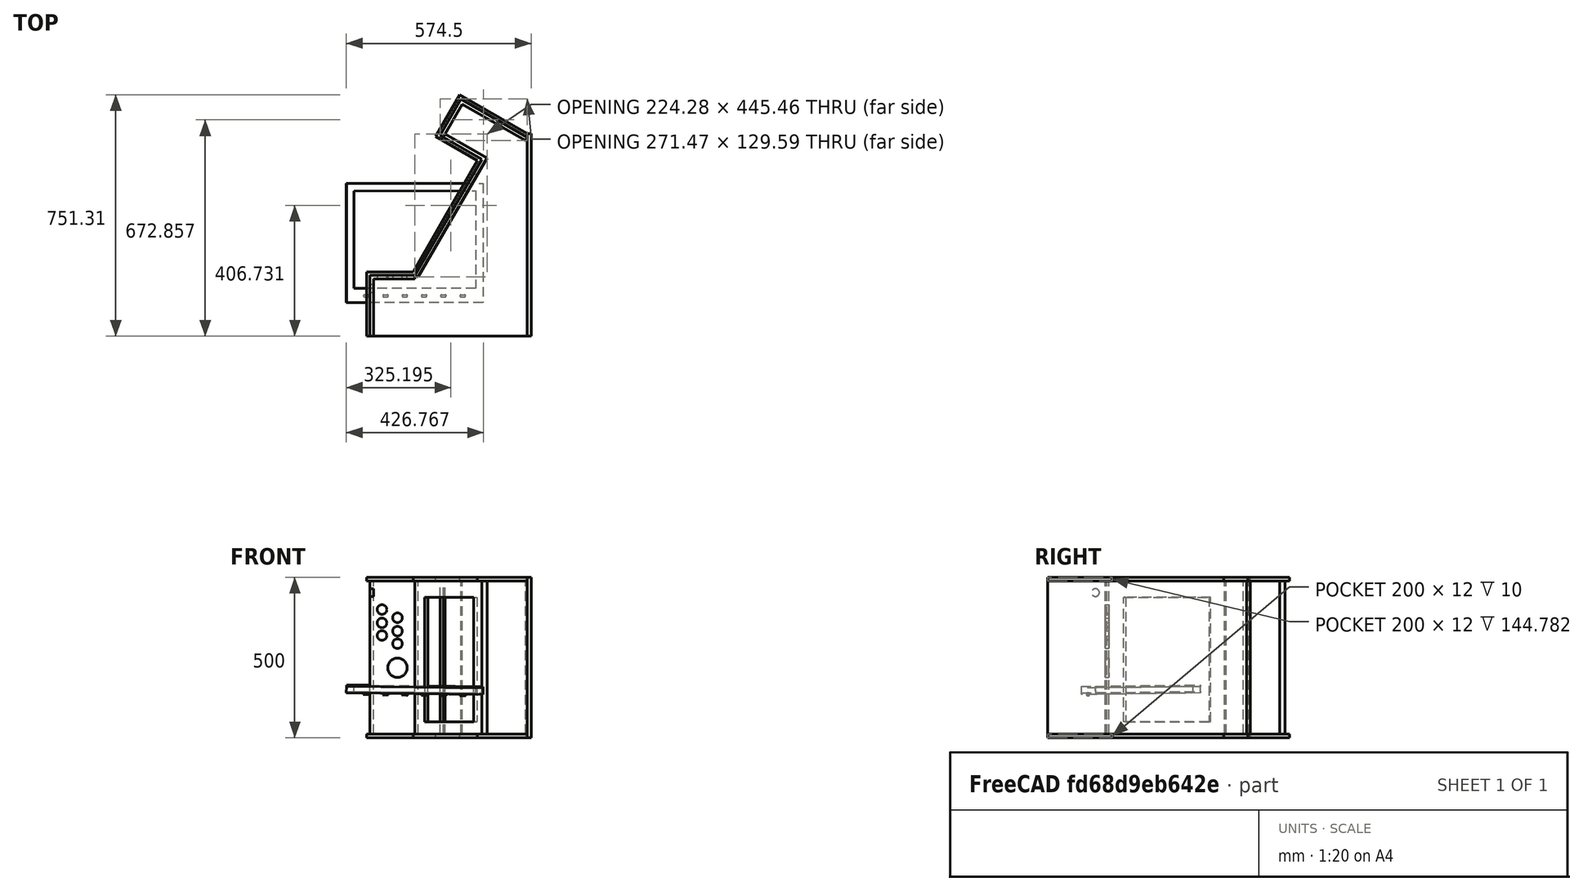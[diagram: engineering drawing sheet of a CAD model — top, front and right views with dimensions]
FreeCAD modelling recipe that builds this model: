
FCSTD DOCUMENT  (FreeCAD 0.17R13541 (Git))
Label: arcadeAvecHautDECO
License: All rights reserved
LicenseURL: http://en.wikipedia.org/wiki/All_rights_reserved
objects: TechDraw::DrawViewDimension×23, Sketcher::SketchObject×8, PartDesign::Pad×5, TechDraw::DrawViewPart×5, Image::ImagePlane×4, PartDesign::Plane×3, PartDesign::Pocket×3, PartDesign::LinearPattern×2, PartDesign::Body×2, TechDraw::DrawViewAnnotation×2, TechDraw::DrawSVGTemplate×1, TechDraw::DrawPage×1
note: 31 computed .brp shape members not serialized (recipe doc carries the construction recipe); baked Part::Feature solids carry a one-line shape summary decoded from their .brp

FEATURE [Sketcher::SketchObject] Sketch  label="coteGauche"
  MapMode = 5
  Support = -> [XY_Plane]
  sketch-geometry (10):
    g0: LineSegment StartX=-500 StartY=200 StartZ=0 EndX=-500 EndY=0 EndZ=0
    g1: LineSegment StartX=-500 StartY=0 StartZ=0 EndX=0 EndY=0 EndZ=0
    g2: LineSegment StartX=0 StartY=0 StartZ=0 EndX=0 EndY=546.41 EndZ=0
    g3: LineSegment [constr] StartX=0 StartY=546.41 StartZ=0 EndX=-155.218 EndY=546.41 EndZ=0
    g4: LineSegment StartX=-155.218 StartY=546.41 StartZ=0 EndX=-355.218 EndY=200 EndZ=0
    g5: LineSegment StartX=-355.218 StartY=200 StartZ=0 EndX=-500 EndY=200 EndZ=0
    g6: LineSegment StartX=-155.218 StartY=546.41 StartZ=0 EndX=-285.122 EndY=621.41 EndZ=0
    g7: LineSegment StartX=-285.122 StartY=621.41 StartZ=0 EndX=-210.122 EndY=751.314 EndZ=0
    g8: LineSegment StartX=-210.122 StartY=751.314 StartZ=0 EndX=0 EndY=630 EndZ=0
    g9: LineSegment StartX=0 StartY=630 StartZ=0 EndX=0 EndY=546.41 EndZ=0
  constraints (28):
    c: Vertical(g0)
    c: Coincident(g0,g1)
    c: Horizontal(g1)
    c: Coincident(g1,g2)
    c: Vertical(g2)
    c: Coincident(g2,g3)
    c: Horizontal(g3)
    c: Coincident(g3,g4)
    c: Coincident(g5,g0)
    c: DistanceX(g1,g1) = 500
    c: DistanceY(g0,g0) = 200
    c: Horizontal(g5)
    c: Coincident(g4,g5)
    c: Coincident(g1,g-1)
    c: Angle(g4,g3) = 2.0944
    c: Distance(g4) = 400
    c: Coincident(g6,g3)
    c: Coincident(g7,g6)
    c: Coincident(g8,g7)
    c: PointOnObject(g8,g-2)
    c: Coincident(g9,g8)
    c: Coincident(g9,g2)
    c: Perpendicular(g6,g7)
    c: Perpendicular(g7,g8)
    c: Perpendicular(g6,g4)
    c: Distance(g6) = 150
    c: Distance(g7) = 150
    c: DistanceY(g1,g8) = 630
FEATURE [PartDesign::Pad] Pad
  Length = 12
  Length2 = 120
  Profile = -> Sketch
  Type = 0
FEATURE [Sketcher::SketchObject] Sketch002  label="arriere"
  ExternalGeometry = -> [Sketch]
  MapMode = 5
  Placement = pos=(0,0,0) rot=(0.57735,0.57735,0.57735;2.0944rad)
  Support = -> [YZ_Plane]
  sketch-geometry (4):
    g0: LineSegment StartX=0 StartY=0 StartZ=0 EndX=0 EndY=500 EndZ=0
    g1: LineSegment StartX=0 StartY=0 StartZ=0 EndX=630 EndY=0 EndZ=0
    g2: LineSegment StartX=630 StartY=0 StartZ=0 EndX=630 EndY=500 EndZ=0
    g3: LineSegment StartX=630 StartY=500 StartZ=0 EndX=0 EndY=500 EndZ=0
  constraints (10):
    c: Vertical(g0)
    c: DistanceY(g0,g0) = 500
    c: Coincident(g0,g-1)
    c: Coincident(g1,g-5)
    c: Coincident(g1,g2)
    c: Vertical(g2)
    c: Coincident(g2,g3)
    c: Coincident(g3,g0)
    c: Perpendicular(g2,g3)
    c: Coincident(g1,g0)
FEATURE [PartDesign::Pad] Pad001
  BaseFeature = -> Pad
  Length = 12
  Length2 = 120
  Profile = -> Sketch002
  Type = 0
FEATURE [PartDesign::LinearPattern] LinearPattern  label="coteDroit"
  BaseFeature = -> Pad001
  Direction = -> Z_Axis
  Length = 488
  Occurrences = 2
  Originals = -> [Pad]
FEATURE [Sketcher::SketchObject] Sketch003  label="Interieur"
  ExternalGeometry = -> [Sketch]
  MapMode = 5
  Support = -> [XY_Plane]
  sketch-geometry (39):
    g0: LineSegment StartX=-490 StartY=190 StartZ=0 EndX=-349.445 EndY=190 EndZ=0
    g1: LineSegment StartX=-349.445 StartY=190 StartZ=0 EndX=-141.558 EndY=550.07 EndZ=0
    g2: LineSegment StartX=-131.166 StartY=544.07 StartZ=0 EndX=-261.069 EndY=619.07 EndZ=0
    g3: LineSegment StartX=-271.465 StartY=625.064 StartZ=0 EndX=-206.462 EndY=737.654 EndZ=0
    g4: LineSegment StartX=-255.069 StartY=629.463 StartZ=0 EndX=-125.166 EndY=554.463 EndZ=0
    g5: LineSegment StartX=-131.166 StartY=544.07 StartZ=0 EndX=-339.052 EndY=184 EndZ=0
    g6: LineSegment StartX=-349.445 StartY=178 StartZ=0 EndX=-490 EndY=178 EndZ=0
    g7: LineSegment StartX=-478 StartY=178 StartZ=0 EndX=-478 EndY=0 EndZ=0
    g8: LineSegment StartX=-478 StartY=0 StartZ=0 EndX=-490 EndY=0 EndZ=0
    g9: LineSegment StartX=-490 StartY=0 StartZ=0 EndX=-490 EndY=178 EndZ=0
    g10: LineSegment StartX=-196.069 StartY=731.654 StartZ=0 EndX=0 EndY=618.453 EndZ=0
    g11: LineSegment StartX=-6 StartY=608.061 StartZ=0 EndX=-202.069 EndY=721.261 EndZ=0
    g12: LineSegment StartX=-196.069 StartY=731.654 StartZ=0 EndX=-261.073 EndY=619.064 EndZ=0
    g13: LineSegment [constr] StartX=-263.064 StartY=426.451 StartZ=0 EndX=-129.787 EndY=349.503 EndZ=0
    g14: GeomPoint X=-225.463 Y=404.742 Z=0
    g15: GeomPoint X=-215.071 Y=398.742 Z=0
    g16: LineSegment [constr] StartX=-133.313 StartY=769.102 StartZ=0 EndX=-285.269 EndY=505.906 EndZ=0
    g17: GeomPoint X=-165.218 Y=713.841 Z=0
    g18: GeomPoint X=-171.218 Y=703.449 Z=0
    g19: GeomPoint X=-224.218 Y=611.65 Z=0
    g20: GeomPoint X=-230.218 Y=601.258 Z=0
    g21: GeomPoint X=-235.218 Y=592.598 Z=0
    g22: GeomPoint X=-160.218 Y=722.502 Z=0
    g23: LineSegment [constr] StartX=-317.542 StartY=758.162 StartZ=0 EndX=-98.31 EndY=631.589 EndZ=0
    g24: GeomPoint X=-234.012 Y=709.936 Z=0
    g25: GeomPoint X=-225.351 Y=704.936 Z=0
    g26: GeomPoint X=-214.959 Y=698.936 Z=0
    g27: GeomPoint X=-234.123 Y=409.742 Z=0
    g28: LineSegment StartX=-349.445 StartY=190 StartZ=0 EndX=-349.445 EndY=178 EndZ=0
    g29: LineSegment StartX=-349.445 StartY=190 StartZ=0 EndX=-339.052 EndY=184 EndZ=0
    g30: LineSegment StartX=0 StartY=618.453 StartZ=0 EndX=-6 EndY=608.061 EndZ=0
    g31: LineSegment StartX=-206.462 StartY=737.654 StartZ=0 EndX=-196.069 EndY=731.654 EndZ=0
    g32: LineSegment StartX=-196.069 StartY=731.654 StartZ=0 EndX=-202.069 EndY=721.261 EndZ=0
    g33: LineSegment StartX=-255.069 StartY=629.463 StartZ=0 EndX=-261.069 EndY=619.07 EndZ=0
    g34: LineSegment StartX=-271.465 StartY=625.064 StartZ=0 EndX=-261.073 EndY=619.064 EndZ=0
    g35: LineSegment StartX=-125.166 StartY=554.463 StartZ=0 EndX=-131.166 EndY=544.07 EndZ=0
    g36: LineSegment StartX=-141.558 StartY=550.07 StartZ=0 EndX=-131.166 EndY=544.07 EndZ=0
    g37: LineSegment StartX=-490 StartY=190 StartZ=0 EndX=-490 EndY=178 EndZ=0
    g38: LineSegment StartX=-490 StartY=178 StartZ=0 EndX=-478 EndY=178 EndZ=0
  constraints (98):
    c: Horizontal(g0)
    c: Coincident(g0,g1)
    c: Horizontal(g6)
    c: PointOnObject(g7,g-1)
    c: Vertical(g7)
    c: Coincident(g7,g8)
    c: PointOnObject(g8,g-1)
    c: Coincident(g8,g9)
    c: Vertical(g9)
    c: Parallel(g1,g-3)
    c: Parallel(g5,g1)
    c: Parallel(g-5,g2)
    c: Parallel(g2,g4)
    c: Parallel(g-6,g3)
    c: Parallel(g3,g12)
    c: Parallel(g-7,g10)
    c: Parallel(g10,g11)
    c: PointOnObject(g10,g-2)
    c: DistanceX(g8,g8) = 12
    c: DistanceY(g6,g0) = 12
    c: DistanceX(g-9,g8) = 10
    c: DistanceY(g0,g-9) = 10
    c: Perpendicular(g-3,g13)
    c: PointOnObject(g14,g1)
    c: PointOnObject(g14,g13)
    c: PointOnObject(g15,g13)
    c: PointOnObject(g15,g5)
    c: Distance(g15,g14) = 12
    c: Perpendicular(g16,g-7)
    c: PointOnObject(g17,g10)
    c: PointOnObject(g18,g11)
    c: PointOnObject(g19,g4)
    c: PointOnObject(g20,g2)
    c: PointOnObject(g17,g16)
    c: PointOnObject(g18,g16)
    c: PointOnObject(g19,g16)
    c: PointOnObject(g20,g16)
    c: Distance(g19,g20) = 12
    c: Distance(g18,g17) = 12
    c: PointOnObject(g21,g-5)
    c: PointOnObject(g22,g-7)
    c: PointOnObject(g22,g16)
    c: PointOnObject(g21,g16)
    c: Distance(g20,g21) = 10
    c: Distance(g17,g22) = 10
    c: Perpendicular(g-6,g23)
    c: PointOnObject(g24,g23)
    c: PointOnObject(g25,g23)
    c: PointOnObject(g24,g-6)
    c: PointOnObject(g25,g3)
    c: PointOnObject(g26,g23)
    c: PointOnObject(g26,g12)
    c: Distance(g26,g25) = 12
    c: Distance(g25,g24) = 10
    c: PointOnObject(g27,g13)
    c: PointOnObject(g27,g-3)
    c: Distance(g14,g27) = 10
    c: Distance(g-3) = 400
    c: Distance(g-6) = 150
    c: DistanceX(g-8,g-8) = 144.782
    c: Distance(g-7) = 242.628
    c: Coincident(g28,g0)
    c: Vertical(g28)
    c: Coincident(g29,g0)
    c: Perpendicular(g5,g29)
    c: Coincident(g6,g28)
    c: Coincident(g5,g29)
    c: Coincident(g30,g10)
    c: Perpendicular(g30,g11)
    c: Coincident(g11,g30)
    c: Coincident(g31,g3)
    c: Coincident(g31,g12)
    c: Perpendicular(g3,g31)
    c: Coincident(g32,g10)
    c: Coincident(g32,g11)
    c: Perpendicular(g10,g32,g10) = 4.71239
    c: Coincident(g12,g10)
    c: Coincident(g33,g4)
    c: Perpendicular(g33,g4)
    c: Coincident(g2,g33)
    c: Coincident(g34,g3)
    c: Coincident(g34,g12)
    c: Perpendicular(g34,g3)
    c: PointOnObject(g4,g12)
    c: Coincident(g35,g4)
    c: Coincident(g35,g2)
    c: Perpendicular(g4,g35,g4) = 4.71239
    c: Coincident(g36,g1)
    c: Coincident(g36,g5)
    c: Perpendicular(g36,g1)
    c: Coincident(g5,g2)
    c: Coincident(g37,g0)
    c: Vertical(g37)
    c: Coincident(g6,g37)
    c: Coincident(g38,g9)
    c: Perpendicular(g38,g9)
    c: Coincident(g38,g7)
    c: Coincident(g6,g9)
FEATURE [PartDesign::Pad] Pad002
  BaseFeature = -> LinearPattern
  Length = 488
  Length2 = 100
  Profile = -> Sketch003
  Type = 0
FEATURE [Sketcher::SketchObject] Sketch007
  MapMode = 5
  Support = -> [XY_Plane001]
  sketch-geometry (8):
    g0: LineSegment StartX=-212.5 StartY=185 StartZ=0 EndX=212.5 EndY=185 EndZ=0
    g1: LineSegment StartX=212.5 StartY=185 StartZ=0 EndX=212.5 EndY=-185 EndZ=0
    g2: LineSegment StartX=212.5 StartY=-185 StartZ=0 EndX=-212.5 EndY=-185 EndZ=0
    g3: LineSegment StartX=-212.5 StartY=-185 StartZ=0 EndX=-212.5 EndY=185 EndZ=0
    g4: LineSegment StartX=-189.5 StartY=162 StartZ=0 EndX=189.5 EndY=162 EndZ=0
    g5: LineSegment StartX=189.5 StartY=162 StartZ=0 EndX=189.5 EndY=-141 EndZ=0
    g6: LineSegment StartX=189.5 StartY=-141 StartZ=0 EndX=-189.5 EndY=-141 EndZ=0
    g7: LineSegment StartX=-189.5 StartY=-141 StartZ=0 EndX=-189.5 EndY=162 EndZ=0
  constraints (22):
    c: Coincident(g0,g1)
    c: Coincident(g1,g2)
    c: Coincident(g2,g3)
    c: Coincident(g3,g0)
    c: Horizontal(g2)
    c: Vertical(g1)
    c: Symmetric(g0,g0,g-2)
    c: Symmetric(g0,g2,g-1)
    c: DistanceY(g1,g0) = 370
    c: DistanceX(g0,g0) = 425
    c: Coincident(g4,g5)
    c: Coincident(g5,g6)
    c: Coincident(g6,g7)
    c: Coincident(g7,g4)
    c: Horizontal(g4)
    c: Horizontal(g6)
    c: Vertical(g5)
    c: Vertical(g7)
    c: DistanceY(g4,g0) = 23
    c: DistanceY(g2,g6) = 44
    c: DistanceX(g4,g0) = 23
    c: DistanceX(g0,g4) = 23
FEATURE [PartDesign::Pad] Pad003
  Length = 20
  Length2 = 100
  Profile = -> Sketch007
  Type = 0
FEATURE [Sketcher::SketchObject] Sketch008
  ExternalGeometry = -> [Sketch007]
  MapMode = 5
  Support = -> [XY_Plane001]
  sketch-geometry (5):
    g0: ArcOfCircle CenterX=-155.799 CenterY=-164.625 CenterZ=0 NormalX=0 NormalY=0 NormalZ=1 AngleXU=0 Radius=3.5 StartAngle=1.5708 EndAngle=4.71239
    g1: ArcOfCircle CenterX=-145.799 CenterY=-164.625 CenterZ=0 NormalX=0 NormalY=0 NormalZ=1 AngleXU=0 Radius=3.5 StartAngle=4.71239 EndAngle=7.85398
    g2: LineSegment StartX=-155.799 StartY=-168.125 StartZ=0 EndX=-145.799 EndY=-168.125 EndZ=0
    g3: LineSegment StartX=-155.799 StartY=-161.125 StartZ=0 EndX=-145.799 EndY=-161.125 EndZ=0
    g4: LineSegment [constr] StartX=-243.041 StartY=-164.625 StartZ=0 EndX=239.075 EndY=-164.625 EndZ=0
  constraints (10):
    c: Tangent(g0,g3) = 1.5708
    c: Tangent(g0,g2) = -1.5708
    c: Tangent(g2,g1) = -1.5708
    c: Tangent(g3,g1) = 1.5708
    c: Horizontal(g2)
    c: Equal(g0,g1)
    c: DistanceY(g0,g0) = 7
    c: DistanceX(g0,g1) = 10
    c: Horizontal(g4)
    c: PointOnObject(g1,g4)
FEATURE [PartDesign::Pad] Pad004  label="bouton"
  BaseFeature = -> Pad003
  Length = 5
  Length2 = 100
  Profile = -> Sketch008
  Reversed = true
  Type = 0
FEATURE [PartDesign::LinearPattern] LinearPattern001
  BaseFeature = -> Pad004
  Direction = -> Sketch008 [H_Axis]
  Length = 300
  Occurrences = 6
  Originals = -> [Pad004]
FEATURE [PartDesign::Body] Body001  label="Ecran"
  Group = -> [Sketch007,Pad003,Sketch008,Pad004,LinearPattern001]
  Origin = -> Origin001
  Placement = pos=(-350,290,140) rot=(0.707107,0.707107,0;0.017453rad)
  Tip = -> LinearPattern001
FEATURE [PartDesign::Plane] DatumPlane
  MapMode = 5
  Placement = pos=(-344.356,198.814,0) rot=(-0.377964,0.654654,0.654654;3.86433rad)
  Support = -> [Pad002]
FEATURE [Sketcher::SketchObject] Sketch009  label="Ecran001"
  ExternalGeometry = -> [Pad002,Sketch003]
  MapMode = 5
  Placement = pos=(-344.356,198.814,0) rot=(-0.377964,0.654654,0.654654;3.86433rad)
  Support = -> [DatumPlane]
  sketch-geometry (4):
    g0: LineSegment StartX=-355.596 StartY=438 StartZ=0 EndX=-50 EndY=438 EndZ=0
    g1: LineSegment StartX=-50 StartY=438 StartZ=0 EndX=-50 EndY=50 EndZ=0
    g2: LineSegment StartX=-50 StartY=50 StartZ=0 EndX=-355.596 EndY=50 EndZ=0
    g3: LineSegment StartX=-355.596 StartY=50 StartZ=0 EndX=-355.596 EndY=438 EndZ=0
  constraints (12):
    c: Coincident(g0,g1)
    c: Coincident(g1,g2)
    c: Coincident(g2,g3)
    c: Coincident(g3,g0)
    c: Horizontal(g0)
    c: Horizontal(g2)
    c: Vertical(g1)
    c: Vertical(g3)
    c: DistanceX(g-5,g2) = 50
    c: DistanceY(g-5,g2) = 50
    c: DistanceX(g1,g-1) = 50
    c: DistanceY(g3,g3) = 388
FEATURE [PartDesign::Plane] DatumPlane001
  MapMode = 5
  Placement = pos=(0,190,0) rot=(0,0.707107,0.707107;3.14159rad)
FEATURE [Sketcher::SketchObject] Sketch011  label="manette"
  MapMode = 5
  Placement = pos=(0,190,0) rot=(0,0.707107,0.707107;3.14159rad)
  Support = -> [DatumPlane001]
  sketch-geometry (9):
    g0: Circle CenterX=403.605 CenterY=218.326 CenterZ=0 NormalX=0 NormalY=0 NormalZ=1 AngleXU=0 Radius=30
    g1: Circle CenterX=403.605 CenterY=293.285 CenterZ=0 NormalX=0 NormalY=0 NormalZ=1 AngleXU=0 Radius=15
    g2: Circle CenterX=403.605 CenterY=332.252 CenterZ=0 NormalX=0 NormalY=0 NormalZ=1 AngleXU=0 Radius=15
    g3: Circle CenterX=403.605 CenterY=373.913 CenterZ=0 NormalX=0 NormalY=0 NormalZ=1 AngleXU=0 Radius=15
    g4: Circle CenterX=451.661 CenterY=357.829 CenterZ=0 NormalX=0 NormalY=0 NormalZ=1 AngleXU=0 Radius=15
    g5: Circle CenterX=451.661 CenterY=318.863 CenterZ=0 NormalX=0 NormalY=0 NormalZ=1 AngleXU=0 Radius=15
    g6: Circle CenterX=451.661 CenterY=399.49 CenterZ=0 NormalX=0 NormalY=0 NormalZ=1 AngleXU=0 Radius=15
    g7: LineSegment [constr] StartX=403.605 StartY=120.684 StartZ=0 EndX=403.605 EndY=527.697 EndZ=0
    g8: LineSegment [constr] StartX=451.661 StartY=111.599 StartZ=0 EndX=451.661 EndY=538.599 EndZ=0
  constraints (16):
    c: Radius(g0) = 30
    c: Radius(g1) = 15
    c: Radius(g2) = 15
    c: Radius(g3) = 15
    c: Radius(g5) = 15
    c: Radius(g4) = 15
    c: Radius(g6) = 15
    c: Vertical(g7)
    c: Vertical(g8)
    c: PointOnObject(g0,g7)
    c: PointOnObject(g1,g7)
    c: PointOnObject(g2,g7)
    c: PointOnObject(g3,g7)
    c: PointOnObject(g5,g8)
    c: PointOnObject(g4,g8)
    c: PointOnObject(g6,g8)
FEATURE [PartDesign::Pocket] Pocket004
  BaseFeature = -> Pad002
  Length = 5
  Length2 = 100
  Profile = -> Sketch011
  Type = 1
FEATURE [PartDesign::Plane] DatumPlane002
  MapMode = 5
  Placement = pos=(-490,0,0) rot=(0.57735,-0.57735,-0.57735;2.0944rad)
  Support = -> [Pocket004]
FEATURE [Sketcher::SketchObject] Sketch012  label="credit"
  MapMode = 5
  Placement = pos=(-490,0,0) rot=(0.57735,-0.57735,-0.57735;2.0944rad)
  Support = -> [DatumPlane002]
  sketch-geometry (1):
    g0: Circle CenterX=-148.426 CenterY=452.331 CenterZ=0 NormalX=0 NormalY=0 NormalZ=1 AngleXU=0 Radius=12
  constraints (1):
    c: Radius(g0) = 12
FEATURE [PartDesign::Pocket] Pocket
  BaseFeature = -> Pocket004
  Length = 0
  Length2 = 100
  Profile = -> Sketch012
  Type = 2
FEATURE [TechDraw::DrawSVGTemplate] Template001
  Height = 210
  Orientation = 1
  Width = 297
FEATURE [TechDraw::DrawViewPart] View  label="Gauche"
  CoarseView = false
  Direction = (0,0,1)
  Focus = 100
  HardHidden = false
  IsoCount = 0
  IsoHidden = false
  IsoVisible = false
  LockPosition = false
  Perspective = false
  Rotation = 0
  Scale = 0.1
  ScaleType = 2
  SeamHidden = false
  SeamVisible = false
  SmoothHidden = false
  SmoothVisible = false
  Source = -> [Pad]
  X = 52.2904
  Y = 139.376
FEATURE [TechDraw::DrawViewDimension] Dimension002
  FormatSpec = %.2f
  LockPosition = false
  MeasureType = 1
  References2D = -> [View]
  Rotation = 0
  ScaleType = 0
  Type = 1
  X = 1.2397
  Y = -46.4916
FEATURE [TechDraw::DrawViewDimension] Dimension004
  FormatSpec = %.2f
  LockPosition = false
  MeasureType = 1
  References2D = -> [View]
  Rotation = 0
  ScaleType = 0
  Type = 1
  X = -38.0185
  Y = -1.42832
FEATURE [TechDraw::DrawViewDimension] Dimension005
  FormatSpec = %.2f
  LockPosition = false
  MeasureType = 1
  References2D = -> [View]
  Rotation = 0
  ScaleType = 0
  Type = 0
  X = 2.22497
  Y = -2.30528
FEATURE [TechDraw::DrawViewDimension] Dimension006
  FormatSpec = %.2f
  LockPosition = false
  MeasureType = 1
  References2D = -> [View]
  Rotation = 0
  ScaleType = 0
  Type = 2
  X = 46.9743
  Y = -2.97556
FEATURE [TechDraw::DrawViewDimension] Dimension007
  FormatSpec = %.2f
  LockPosition = false
  MeasureType = 1
  References2D = -> [View]
  Rotation = 0
  ScaleType = 0
  Type = 1
  X = 40.5884
  Y = 56.5644
FEATURE [TechDraw::DrawViewDimension] Dimension008
  FormatSpec = %.2f
  LockPosition = false
  MeasureType = 1
  References2D = -> [View]
  Rotation = 0
  ScaleType = 0
  Type = 2
  X = 59.1292
  Y = -4.46353
FEATURE [TechDraw::DrawViewDimension] Dimension009
  FormatSpec = %.2f
  LockPosition = false
  MeasureType = 1
  References2D = -> [View]
  Rotation = 0
  ScaleType = 0
  Type = 2
  X = -47.4876
  Y = 55.7916
FEATURE [TechDraw::DrawViewDimension] Dimension010
  FormatSpec = %.2f
  LockPosition = false
  MeasureType = 1
  References2D = -> [View]
  Rotation = 0
  ScaleType = 0
  Type = 2
  X = 34.4065
  Y = -2.69152
FEATURE [TechDraw::DrawViewDimension] Dimension011
  FormatSpec = %.2f
  LockPosition = false
  MeasureType = 1
  References2D = -> [View]
  Rotation = 0
  ScaleType = 0
  Type = 1
  X = 40.2434
  Y = 45.5732
FEATURE [TechDraw::DrawViewDimension] Dimension012
  FormatSpec = %.2f
  LockPosition = false
  MeasureType = 1
  References2D = -> [View]
  Rotation = 0
  ScaleType = 0
  Type = 1
  X = 39.9285
  Y = 65.8633
FEATURE [TechDraw::DrawViewDimension] Dimension013
  FormatSpec = %.2f
  LockPosition = false
  MeasureType = 1
  References2D = -> [View]
  Rotation = 0
  ScaleType = 0
  Type = 2
  X = -39.4563
  Y = -54.3469
FEATURE [TechDraw::DrawViewDimension] Dimension016
  FormatSpec = %.2f
  LockPosition = false
  MeasureType = 1
  References2D = -> [View]
  Rotation = 0
  ScaleType = 0
  Type = 0
  X = -25.6294
  Y = 14.8167
FEATURE [TechDraw::DrawViewAnnotation] Annotation  label="Dimensions"
  Font = Times New Roman
  LineSpace = 80
  LockPosition = false
  MaxWidth = -1
  Rotation = 0
  ScaleType = 0
  Text = : (2) 50,0x75,1 | : (1) 50,0x63,0 | : (1) 47,6x13,0 | : (1) 47,6x17,8 | : (1) 47,6x14,1 | : (1) 47,6x15,0 | : (1) 47,6x22,6 | : (1) 47,6x41,6
  TextSize = 4
  TextStyle = 0
  X = 264.695
  Y = 36.1066
FEATURE [TechDraw::DrawViewAnnotation] Annotation001  label="Description"
  Font = Times New Roman
  LineSpace = 80
  LockPosition = false
  MaxWidth = -1
  Rotation = 0
  ScaleType = 0
  Text = Cotes | Arriere | Face Haut | Face bas | Face Hori | Face Dessous | Dessus | Ecran
  TextSize = 4
  TextStyle = 0
  X = 224.235
  Y = 36.6774
FEATURE [PartDesign::Pocket] Pocket005
  BaseFeature = -> Pocket
  Length = 5
  Length2 = 100
  Profile = -> Sketch009
  Type = 2
FEATURE [PartDesign::Body] Body  label="socle"
  Group = -> [Sketch,Pad,Sketch002,Pad001,LinearPattern,Sketch003,Pad002,DatumPlane,Sketch009,DatumPlane001,Sketch011,Pocket004,DatumPlane002,Sketch012,Pocket,Pocket005]
  Origin = -> Origin
  Tip = -> Pocket005
FEATURE [TechDraw::DrawViewPart] View005  label="Devant"
  CoarseView = false
  Direction = (-1,0,0)
  Focus = 100
  HardHidden = false
  IsoCount = 0
  IsoHidden = false
  IsoVisible = false
  LockPosition = false
  Perspective = false
  Rotation = 90
  Scale = 0.1
  ScaleType = 2
  SeamHidden = false
  SeamVisible = false
  SmoothHidden = false
  SmoothVisible = false
  Source = -> [Pocket005]
  X = 153.754
  Y = 140.395
FEATURE [TechDraw::DrawViewDimension] Dimension
  FormatSpec = %.2f
  LockPosition = false
  MeasureType = 1
  References2D = -> [View005]
  Rotation = 0
  ScaleType = 0
  Type = 1
  X = 2.7101
  Y = -51.8326
FEATURE [TechDraw::DrawViewPart] View007  label="Interieur001"
  CoarseView = false
  Direction = (0,0,1)
  Focus = 100
  HardHidden = false
  IsoCount = 0
  IsoHidden = false
  IsoVisible = false
  LockPosition = false
  Perspective = false
  Rotation = 0
  Scale = 0.1
  ScaleType = 0
  SeamHidden = false
  SeamVisible = false
  SmoothHidden = false
  SmoothVisible = false
  Source = -> [Sketch003]
  X = 231.044
  Y = 141.35
FEATURE [TechDraw::DrawViewDimension] Dimension017
  FormatSpec = %.2f
  LockPosition = false
  MeasureType = 1
  References2D = -> [View007]
  Rotation = 0
  ScaleType = 0
  Type = 2
  X = -38.1342
  Y = -27.374
FEATURE [TechDraw::DrawViewDimension] Dimension018
  FormatSpec = %.2f
  LockPosition = false
  MeasureType = 1
  References2D = -> [View007]
  Rotation = 0
  ScaleType = 0
  Type = 1
  X = -18.0809
  Y = -5.34406
FEATURE [TechDraw::DrawViewDimension] Dimension019
  FormatSpec = %.2f
  LockPosition = false
  MeasureType = 1
  References2D = -> [View007]
  Rotation = 0
  ScaleType = 0
  Type = 0
  X = 7.31928
  Y = -4.37466
FEATURE [TechDraw::DrawViewDimension] Dimension021
  FormatSpec = %.2f
  LockPosition = false
  MeasureType = 1
  References2D = -> [View007]
  Rotation = 0
  ScaleType = 0
  Type = 0
  X = -27.2664
  Y = 48.0649
FEATURE [TechDraw::DrawViewDimension] Dimension022
  FormatSpec = %.2f
  LockPosition = false
  MeasureType = 1
  References2D = -> [View007]
  Rotation = 0
  ScaleType = 0
  Type = 0
  X = 19.079
  Y = 40.9701
FEATURE [TechDraw::DrawViewDimension] Dimension023
  FormatSpec = %.2f
  LockPosition = false
  MeasureType = 1
  References2D = -> [View007]
  Rotation = 0
  ScaleType = 0
  Type = 1
  X = -6.97894
  Y = -45.0389
FEATURE [TechDraw::DrawViewDimension] Dimension024
  FormatSpec = %.2f
  LockPosition = false
  MeasureType = 1
  References2D = -> [View007]
  Rotation = 0
  ScaleType = 0
  Type = 0
  X = 0.017436
  Y = 16.6939
FEATURE [TechDraw::DrawViewPart] View008  label="3D"
  CoarseView = true
  Direction = (-0.776,0.389,0.496)
  Focus = 100
  HardHidden = true
  IsoCount = 0
  IsoHidden = true
  IsoVisible = false
  LockPosition = false
  Perspective = true
  Rotation = 90
  Scale = 0.09
  ScaleType = 0
  SeamHidden = false
  SeamVisible = false
  SmoothHidden = false
  SmoothVisible = false
  Source = -> [Pocket005]
  X = 61.2755
  Y = 45.4138
FEATURE [TechDraw::DrawViewPart] View009  label="Dessus"
  CoarseView = false
  Direction = (0,1,0)
  Focus = 100
  HardHidden = false
  IsoCount = 0
  IsoHidden = false
  IsoVisible = false
  LockPosition = false
  Perspective = false
  Rotation = 90
  Scale = 0.1
  ScaleType = 0
  SeamHidden = false
  SeamVisible = false
  SmoothHidden = false
  SmoothVisible = false
  Source = -> [Pocket005]
  X = 154.593
  Y = 47.6741
FEATURE [TechDraw::DrawViewDimension] Dimension025
  FormatSpec = %.2f
  LockPosition = false
  MeasureType = 1
  References2D = -> [View]
  Rotation = 0
  ScaleType = 0
  Type = 2
  X = 33.5959
  Y = 29.8129
FEATURE [TechDraw::DrawViewDimension] Dimension026
  FormatSpec = %.2f
  LockPosition = false
  MeasureType = 1
  References2D = -> [View]
  Rotation = 0
  ScaleType = 0
  Type = 2
  X = 46.8955
  Y = 30.3923
FEATURE [TechDraw::DrawViewDimension] Dimension027
  FormatSpec = %.2f
  LockPosition = false
  MeasureType = 1
  References2D = -> [View]
  Rotation = 0
  ScaleType = 0
  Type = 0
  X = -22.471
  Y = 63.4721
FEATURE [TechDraw::DrawPage] Page001
  KeepUpdated = true
  ProjectionType = 0
  Template = -> Template001
  Views = -> [View,Dimension002,Dimension004,Dimension005,Dimension006,Dimension007,Dimension008,Dimension009,Dimension010,Dimension011,Dimension012,Dimension013,Dimension016,Annotation,Annotation001,View005,Dimension,View007,Dimension017,Dimension018,Dimension019,Dimension021,Dimension022,Dimension023,Dimension024,View008,View009,Dimension025,Dimension026,Dimension027]
FEATURE [Image::ImagePlane] ImagePlane001
  Placement = pos=(-119,277,-13) rot=(0,-1,0;3.14159rad)
  XSize = 203
  YSize = 517
FEATURE [Image::ImagePlane] ImagePlane
  Placement = pos=(-127,260,508) rot=(0,0,1;0rad)
  XSize = 213
  YSize = 477
FEATURE [Image::ImagePlane] ImagePlane004
  Placement = pos=(-493.446,106,194.412) rot=(0,-1,0;1.5708rad)
  XSize = 128
  YSize = 152
FEATURE [Image::ImagePlane] ImagePlane005
  Placement = pos=(12,298.989,287.957) rot=(0,-1,0;4.71239rad)
  XSize = 370
  YSize = 546
